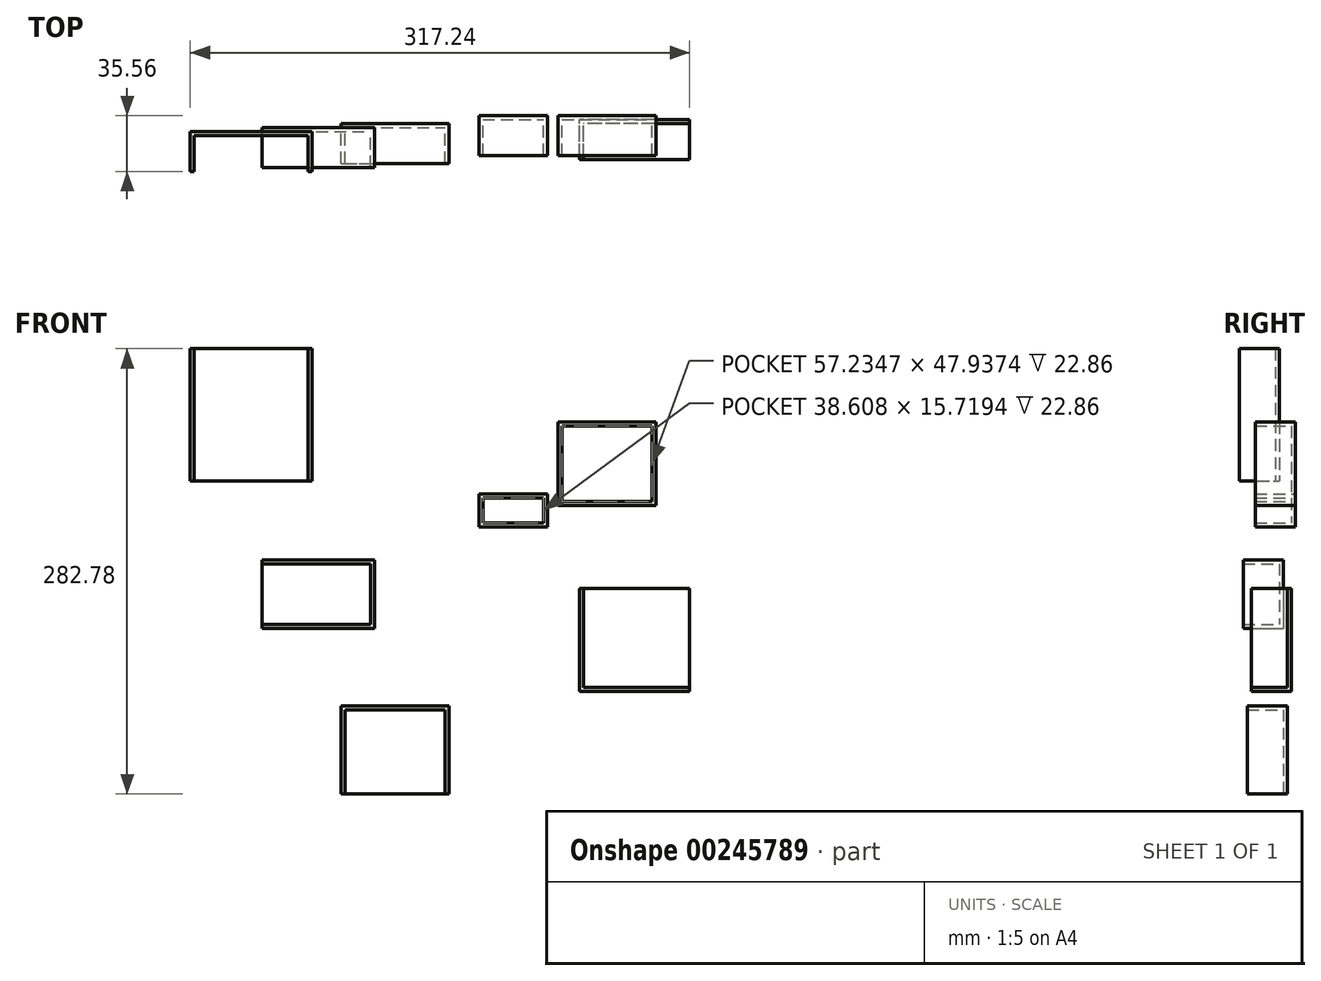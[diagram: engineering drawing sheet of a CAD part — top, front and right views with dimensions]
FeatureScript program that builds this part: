
annotation { "Feature Type Name" : "Feature", "Feature Type Description" : "" }
export const myFeature = defineFeature(function(context is Context, id is Id, definition is map)
    precondition{}
    {
        {
            var Q0;
            Q0=qCreatedBy(makeId("Front.planeOp"),FACE);
            var sketch = newSketch(context, id + "F0", { "sketchPlane" : qUnion([Q0])});
            skLineSegment(sketch, "E0.bottom", {"start": v(-43.69, 59.86) * mm, "end": v(0, 59.86) * mm});
            skLineSegment(sketch, "E0.top", {"start": v(-43.69, 39.06) * mm, "end": v(0, 39.06) * mm});
            skLineSegment(sketch, "E0.left", {"start": v(-43.69, 59.86) * mm, "end": v(-43.69, 39.06) * mm});
            skLineSegment(sketch, "E0.right", {"start": v(0, 59.86) * mm, "end": v(0, 39.06) * mm});
            skLineSegment(sketch, "E1.bottom", {"start": v(6.6, 105.7) * mm, "end": v(68.92, 105.7) * mm});
            skLineSegment(sketch, "E1.top", {"start": v(6.6, 52.7) * mm, "end": v(68.92, 52.7) * mm});
            skLineSegment(sketch, "E1.left", {"start": v(6.6, 105.7) * mm, "end": v(6.6, 52.7) * mm});
            skLineSegment(sketch, "E1.right", {"start": v(68.92, 105.7) * mm, "end": v(68.92, 52.7) * mm});
            skSolve(sketch);
        }
        {
            var Q0;
            Q0 = qSketchRegion(id + "F0", true);
            extrude(context, id + "F1", {"entities" : qUnion([Q0]), "depth" : 25.4 * mm});
        }
        {
            var Q0;
            Q0=makeQuery(id+"F1.opExtrude","CAP_FACE",FACE,{"disambiguationData":[OSD([sQuery(id+"F0.wireOp",EDGE,"E1.bottom"),sQuery(id+"F0.wireOp",EDGE,"E1.top"),sQuery(id+"F0.wireOp",EDGE,"E1.left"),sQuery(id+"F0.wireOp",EDGE,"E1.right")])],"isStart":false});
            var Q1;
            Q1=makeQuery(id+"F1.opExtrude","CAP_FACE",FACE,{"disambiguationData":[OSD([sQuery(id+"F0.wireOp",EDGE,"E0.bottom"),sQuery(id+"F0.wireOp",EDGE,"E0.top"),sQuery(id+"F0.wireOp",EDGE,"E0.left"),sQuery(id+"F0.wireOp",EDGE,"E0.right")])],"isStart":false});
            shell(context, id + "F11", {"entities" : qUnion([Q0, Q1]), "thickness" : 2.54 * mm});
        }
        {
            var Q0;
            Q0=makeQuery(id+"F11.opShell","OFFSET_FACE",FACE,{"disambiguationData":[OSD([sQuery(id+"F0.wireOp",EDGE,"E1.bottom"),sQuery(id+"F0.wireOp",EDGE,"E1.top"),sQuery(id+"F0.wireOp",EDGE,"E1.left"),sQuery(id+"F0.wireOp",EDGE,"E1.right")])]});
            var sketch = newSketch(context, id + "F2", { "sketchPlane" : qUnion([Q0])});
            skLineSegment(sketch, "E2.bottom", {"start": v(90.2, 0) * mm, "end": v(20.1, 0) * mm});
            skLineSegment(sketch, "E2.top", {"start": v(90.2, -65.53) * mm, "end": v(20.1, -65.53) * mm});
            skLineSegment(sketch, "E2.left", {"start": v(90.2, 0) * mm, "end": v(90.2, -65.53) * mm});
            skLineSegment(sketch, "E2.right", {"start": v(20.1, 0) * mm, "end": v(20.1, -65.53) * mm});
            skPoint(sketch, "E2.middle", {"position": v(55.15, -32.76) * mm});
            skSolve(sketch);
        }
        {
            var Q0;
            Q0 = qSketchRegion(id + "F2", true);
            extrude(context, id + "F3", {"entities" : qUnion([Q0]), "depth" : 25.4 * mm});
        }
        {
            var Q0;
            Q0=makeQuery(id+"F3.opExtrude","SWEPT_FACE",FACE,{"disambiguationData":[OSD([sQuery(id+"F2.wireOp",EDGE,"E2.left")])]});
            var Q1;
            Q1=makeQuery(id+"F3.opExtrude","SWEPT_FACE",FACE,{"disambiguationData":[OSD([sQuery(id+"F2.wireOp",EDGE,"E2.bottom")])]});
            var Q2;
            Q2=makeQuery(id+"F3.opExtrude","CAP_FACE",FACE,{"disambiguationData":[OSD([sQuery(id+"F2.wireOp",EDGE,"E2.bottom"),sQuery(id+"F2.wireOp",EDGE,"E2.top"),sQuery(id+"F2.wireOp",EDGE,"E2.left"),sQuery(id+"F2.wireOp",EDGE,"E2.right")])],"isStart":false});
            shell(context, id + "F4", {"entities" : qUnion([Q0, Q1, Q2]), "thickness" : 2.54 * mm});
        }
        {
            var Q0;
            Q0=makeQuery(id+"F4.opShell","OFFSET_FACE",FACE,{"disambiguationData":[OSD([sQuery(id+"F2.wireOp",EDGE,"E2.bottom"),sQuery(id+"F2.wireOp",EDGE,"E2.top"),sQuery(id+"F2.wireOp",EDGE,"E2.left"),sQuery(id+"F2.wireOp",EDGE,"E2.right")])]});
            var sketch = newSketch(context, id + "F5", { "sketchPlane" : qUnion([Q0])});
            skLineSegment(sketch, "E3.bottom", {"start": v(-131.23, -74.48) * mm, "end": v(-62.68, -74.48) * mm});
            skLineSegment(sketch, "E3.top", {"start": v(-131.23, -130.52) * mm, "end": v(-62.68, -130.52) * mm});
            skLineSegment(sketch, "E3.left", {"start": v(-131.23, -74.48) * mm, "end": v(-131.23, -130.52) * mm});
            skLineSegment(sketch, "E3.right", {"start": v(-62.68, -74.48) * mm, "end": v(-62.68, -130.52) * mm});
            skSolve(sketch);
        }
        {
            var Q0;
            Q0 = qSketchRegion(id + "F5", true);
            extrude(context, id + "F6", {"entities" : qUnion([Q0]), "depth" : 25.4 * mm});
        }
        {
            var Q0;
            Q0=makeQuery(id+"F6.opExtrude","CAP_FACE",FACE,{"disambiguationData":[OSD([sQuery(id+"F5.wireOp",EDGE,"E3.bottom"),sQuery(id+"F5.wireOp",EDGE,"E3.top"),sQuery(id+"F5.wireOp",EDGE,"E3.left"),sQuery(id+"F5.wireOp",EDGE,"E3.right")])],"isStart":false});
            var Q1;
            Q1=makeQuery(id+"F6.opExtrude","SWEPT_FACE",FACE,{"disambiguationData":[OSD([sQuery(id+"F5.wireOp",EDGE,"E3.top")])]});
            shell(context, id + "F7", {"entities" : qUnion([Q0, Q1]), "thickness" : 2.54 * mm});
        }
        {
            var Q0;
            Q0=makeQuery(id+"F7.opShell","OFFSET_FACE",FACE,{"disambiguationData":[OSD([sQuery(id+"F5.wireOp",EDGE,"E3.bottom"),sQuery(id+"F5.wireOp",EDGE,"E3.top"),sQuery(id+"F5.wireOp",EDGE,"E3.left"),sQuery(id+"F5.wireOp",EDGE,"E3.right")])]});
            var sketch = newSketch(context, id + "F8", { "sketchPlane" : qUnion([Q0])});
            skLineSegment(sketch, "E4.bottom", {"start": v(-181.48, 18.12) * mm, "end": v(-109.92, 18.12) * mm});
            skLineSegment(sketch, "E4.top", {"start": v(-181.48, -25.48) * mm, "end": v(-109.92, -25.48) * mm});
            skLineSegment(sketch, "E4.left", {"start": v(-181.48, 18.12) * mm, "end": v(-181.48, -25.48) * mm});
            skLineSegment(sketch, "E4.right", {"start": v(-109.92, 18.12) * mm, "end": v(-109.92, -25.48) * mm});
            skSolve(sketch);
        }
        {
            var Q0;
            Q0 = qSketchRegion(id + "F8", true);
            extrude(context, id + "F12", {"entities" : qUnion([Q0]), "depth" : 25.4 * mm});
        }
        {
            var Q0;
            Q0=makeQuery(id+"F12.opExtrude","SWEPT_FACE",FACE,{"disambiguationData":[OSD([sQuery(id+"F8.wireOp",EDGE,"E4.left")])]});
            var Q1;
            Q1=makeQuery(id+"F12.opExtrude","CAP_FACE",FACE,{"disambiguationData":[OSD([sQuery(id+"F8.wireOp",EDGE,"E4.bottom"),sQuery(id+"F8.wireOp",EDGE,"E4.top"),sQuery(id+"F8.wireOp",EDGE,"E4.left"),sQuery(id+"F8.wireOp",EDGE,"E4.right")])],"isStart":false});
            shell(context, id + "F13", {"entities" : qUnion([Q0, Q1]), "thickness" : 2.54 * mm});
        }
        {
            var Q0;
            Q0=makeQuery(id+"F13.opShell","OFFSET_FACE",FACE,{"disambiguationData":[OSD([sQuery(id+"F8.wireOp",EDGE,"E4.bottom"),sQuery(id+"F8.wireOp",EDGE,"E4.top"),sQuery(id+"F8.wireOp",EDGE,"E4.left"),sQuery(id+"F8.wireOp",EDGE,"E4.right")])]});
            var sketch = newSketch(context, id + "F9", { "sketchPlane" : qUnion([Q0])});
            skLineSegment(sketch, "E5.bottom", {"start": v(-149.6, 152.26) * mm, "end": v(-227.04, 152.26) * mm});
            skLineSegment(sketch, "E5.top", {"start": v(-149.6, 68.17) * mm, "end": v(-227.04, 68.17) * mm});
            skLineSegment(sketch, "E5.left", {"start": v(-149.6, 152.26) * mm, "end": v(-149.6, 68.17) * mm});
            skLineSegment(sketch, "E5.right", {"start": v(-227.04, 152.26) * mm, "end": v(-227.04, 68.17) * mm});
            skSolve(sketch);
        }
        {
            var Q0;
            Q0 = qSketchRegion(id + "F9", true);
            extrude(context, id + "F10", {"entities" : qUnion([Q0]), "depth" : 25.4 * mm});
        }
        {
            var Q0;
            Q0=makeQuery(id+"F10.opExtrude","CAP_FACE",FACE,{"disambiguationData":[OSD([sQuery(id+"F9.wireOp",EDGE,"E5.bottom"),sQuery(id+"F9.wireOp",EDGE,"E5.top"),sQuery(id+"F9.wireOp",EDGE,"E5.left"),sQuery(id+"F9.wireOp",EDGE,"E5.right")])],"isStart":false});
            var Q1;
            Q1=makeQuery(id+"F10.opExtrude","SWEPT_FACE",FACE,{"disambiguationData":[OSD([sQuery(id+"F9.wireOp",EDGE,"E5.top")])]});
            var Q2;
            Q2=makeQuery(id+"F10.opExtrude","SWEPT_FACE",FACE,{"disambiguationData":[OSD([sQuery(id+"F9.wireOp",EDGE,"E5.bottom")])]});
            shell(context, id + "F14", {"entities" : qUnion([Q0, Q1, Q2]), "thickness" : 2.54 * mm});
        }
    });
